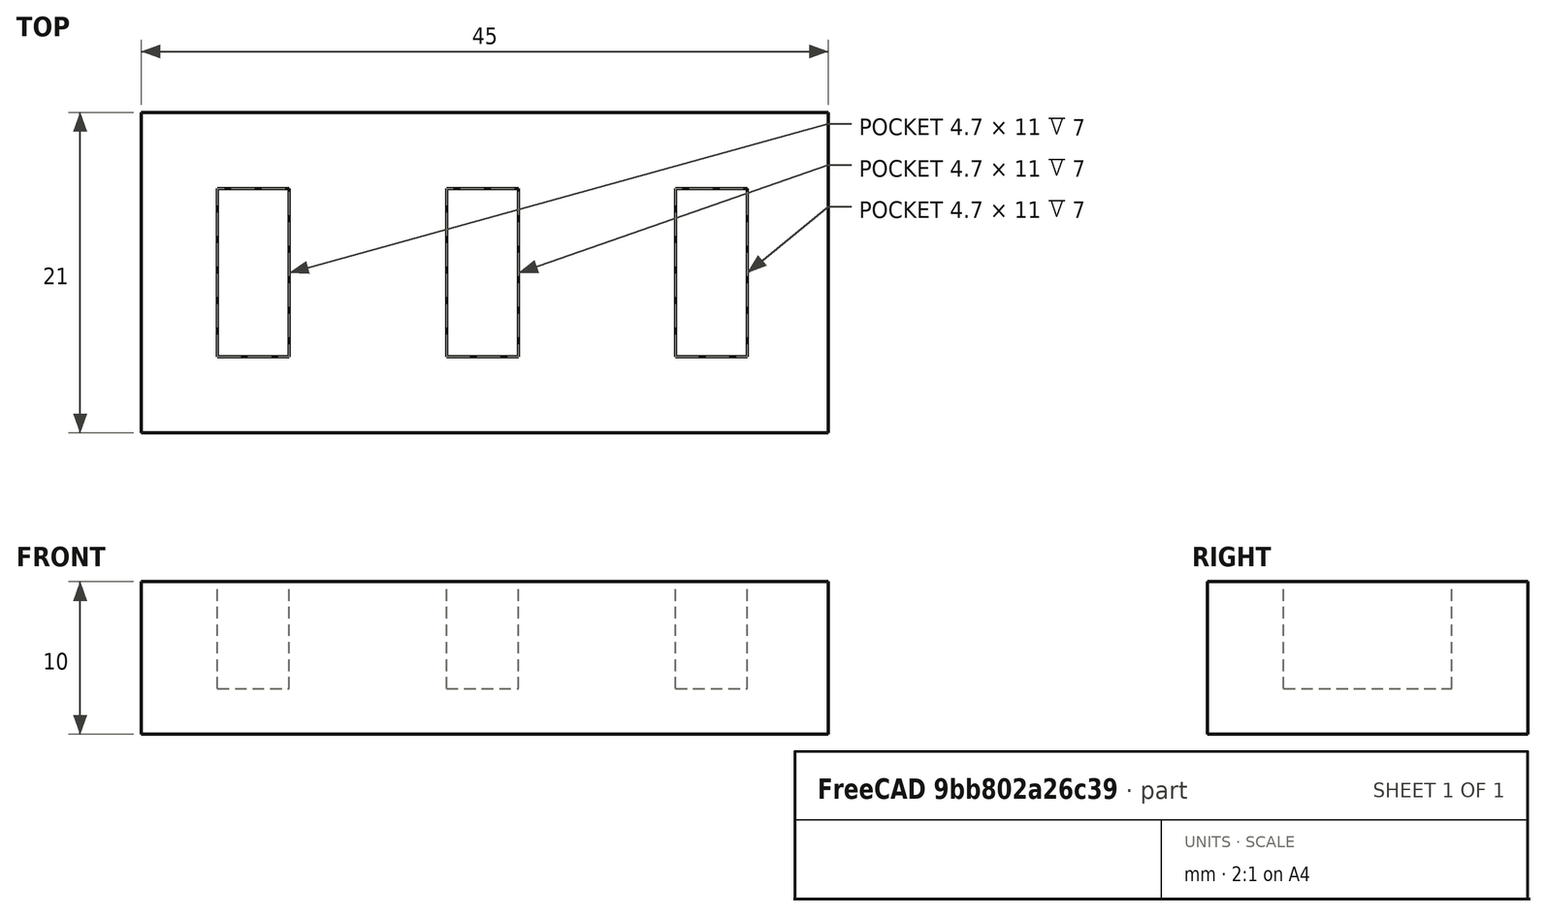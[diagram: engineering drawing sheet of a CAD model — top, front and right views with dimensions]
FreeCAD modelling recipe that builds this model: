
FCSTD DOCUMENT  (FreeCAD 1.0R39319 (Git))
Label: ojt1_t08p01_usb_flash
License: All rights reserved
LicenseURL: https://en.wikipedia.org/wiki/All_rights_reserved
objects: Part::Box×4, Part::MultiFuse×1, Part::Cut×1
note: 6 computed .brp shape members not serialized (recipe doc carries the construction recipe); baked Part::Feature solids carry a one-line shape summary decoded from their .brp

FEATURE [Part::Box] Box  label="Ranura-1"
  AttacherType = Attacher::AttachEngine3D
  Height = 12
  Length = 4.7
  Width = 11
FEATURE [Part::Box] Box001  label="Ranura-2"
  AttacherType = Attacher::AttachEngine3D
  Height = 12
  Length = 4.7
  Placement = pos=(15,0,0) rot=(0,0,1;0rad)
  Width = 11
FEATURE [Part::Box] Box002  label="Ranura-3"
  AttacherType = Attacher::AttachEngine3D
  Height = 12
  Length = 4.7
  Placement = pos=(30,0,0) rot=(0,0,1;0rad)
  Width = 11
FEATURE [Part::MultiFuse] Fusion  label="Ranuras"
  Placement = pos=(5,5,3) rot=(0,0,1;0rad)
  Refine = true
  Shapes = -> [Box,Box001,Box002]
FEATURE [Part::Box] Box003  label="Base"
  AttacherType = Attacher::AttachEngine3D
  Height = 10
  Length = 45
  Width = 21
FEATURE [Part::Cut] Cut  label="Porta-pendrives"
  Base = -> Box003
  Refine = true
  Tool = -> Fusion
